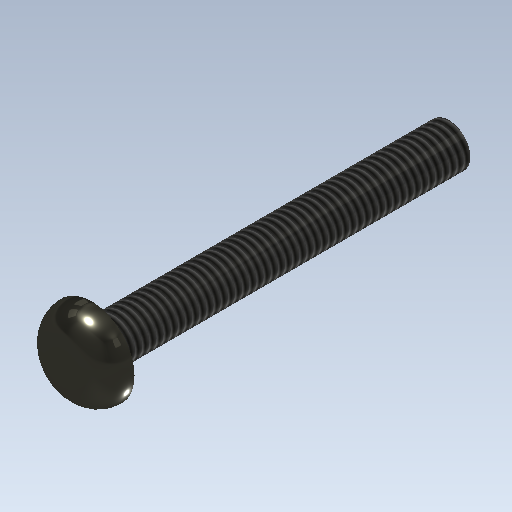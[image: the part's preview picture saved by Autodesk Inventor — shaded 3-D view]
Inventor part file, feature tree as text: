
AUTODESK INVENTOR PART (.ipt)
format: ipt  version: 2020.2 (Build 242310000, 310)  size: 161,792 bytes
history: native  units: mm
features: extrude x4, sketch x4, other x1, fillet x1, thread x1
ambient origin geometry x1: Origin
bodies: Body1 (feature_tree)
feature tree (11):
  other  "ソリッド1"
  extrude  "押し出し1"  Depth=3.0mm
  extrude  "押し出し2"  Depth=6.0mm TaperAngle=0.0deg
  fillet  "フィレット1"  Radius=6.0mm
  thread  "ねじ1"
  extrude  "押し出し3"  Depth=2.0mm TaperAngle=0.0deg
  extrude  "押し出し4"  Depth=2.0mm
  sketch  "スケッチ1"
  sketch  "スケッチ2"
  sketch  "スケッチ3"
  sketch  "スケッチ4"
